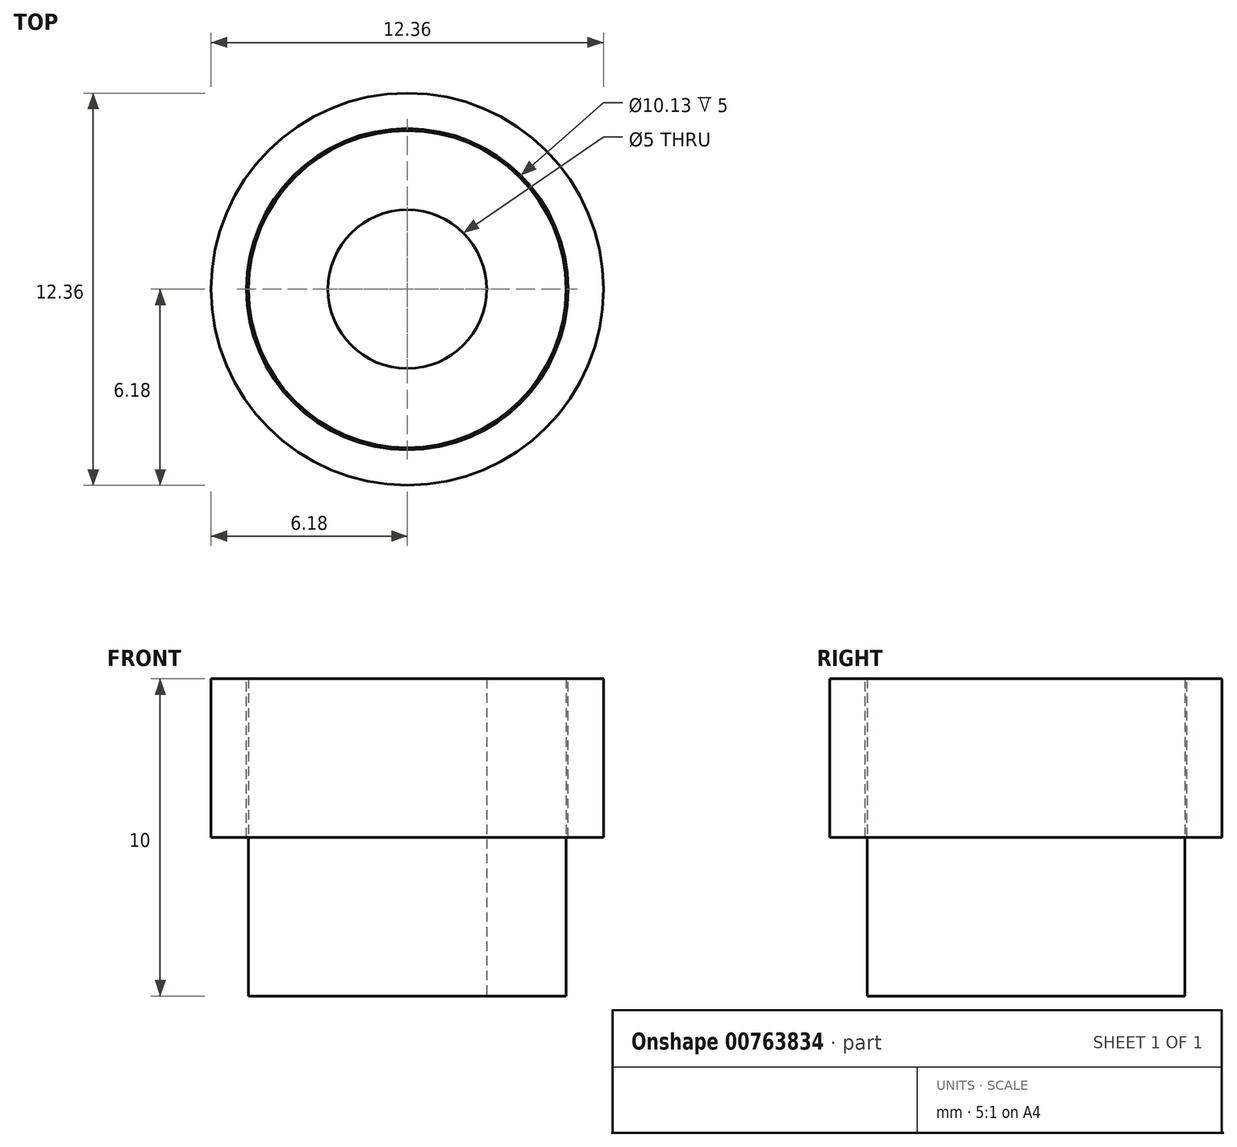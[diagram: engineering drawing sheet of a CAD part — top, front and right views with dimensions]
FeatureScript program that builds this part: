
annotation { "Feature Type Name" : "Feature", "Feature Type Description" : "" }
export const myFeature = defineFeature(function(context is Context, id is Id, definition is map)
    precondition{}
    {
        {
            var Q0;
            Q0=qCreatedBy(makeId("Top.planeOp"),FACE);
            var sketch = newSketch(context, id + "F0", { "sketchPlane" : qUnion([Q0])});
            skCircle(sketch, "E0", {"center": v(0, 0) * mm, "radius": 5 * mm});
            skCircle(sketch, "E1", {"center": v(0, 0) * mm, "radius": 2.5 * mm});
            skSolve(sketch);
        }
        {
            var Q0;
            Q0=makeQuery(id+"F0.imprint","IMPRINT",FACE,{"disambiguationData":[TD([[makeQuery(id+"F0.imprint","IMPRINT",EDGE,{"derivedFrom":sQuery(id+"F0.wireOp",EDGE,"E0")}),1.0]])]});
            extrude(context, id + "F1", {"entities" : qUnion([Q0]), "depth" : 10 * mm, "offsetDistance" : 25 * mm});
        }
        {
            var Q0;
            Q0=makeQuery(id+"F1.opExtrude","CAP_FACE",FACE,{"disambiguationData":[OSD([sQuery(id+"F0.wireOp",EDGE,"E0"),sQuery(id+"F0.wireOp",EDGE,"E1")])],"isStart":false});
            var sketch = newSketch(context, id + "F2", { "sketchPlane" : qUnion([Q0])});
            skCircle(sketch, "E2", {"center": v(0, 0) * mm, "radius": 6.18 * mm});
            skCircle(sketch, "E3", {"center": v(0, 0) * mm, "radius": 5.07 * mm});
            skSolve(sketch);
        }
        {
            var Q0;
            Q0=makeQuery(id+"F2.imprint","IMPRINT",FACE,{"disambiguationData":[TD([[makeQuery(id+"F2.imprint","IMPRINT",EDGE,{"derivedFrom":sQuery(id+"F2.wireOp",EDGE,"E2")}),1.0]])]});
            extrude(context, id + "F3", {"entities" : qUnion([Q0]), "oppositeDirection" : true, "depth" : 5 * mm, "offsetDistance" : 25 * mm});
        }
    });
